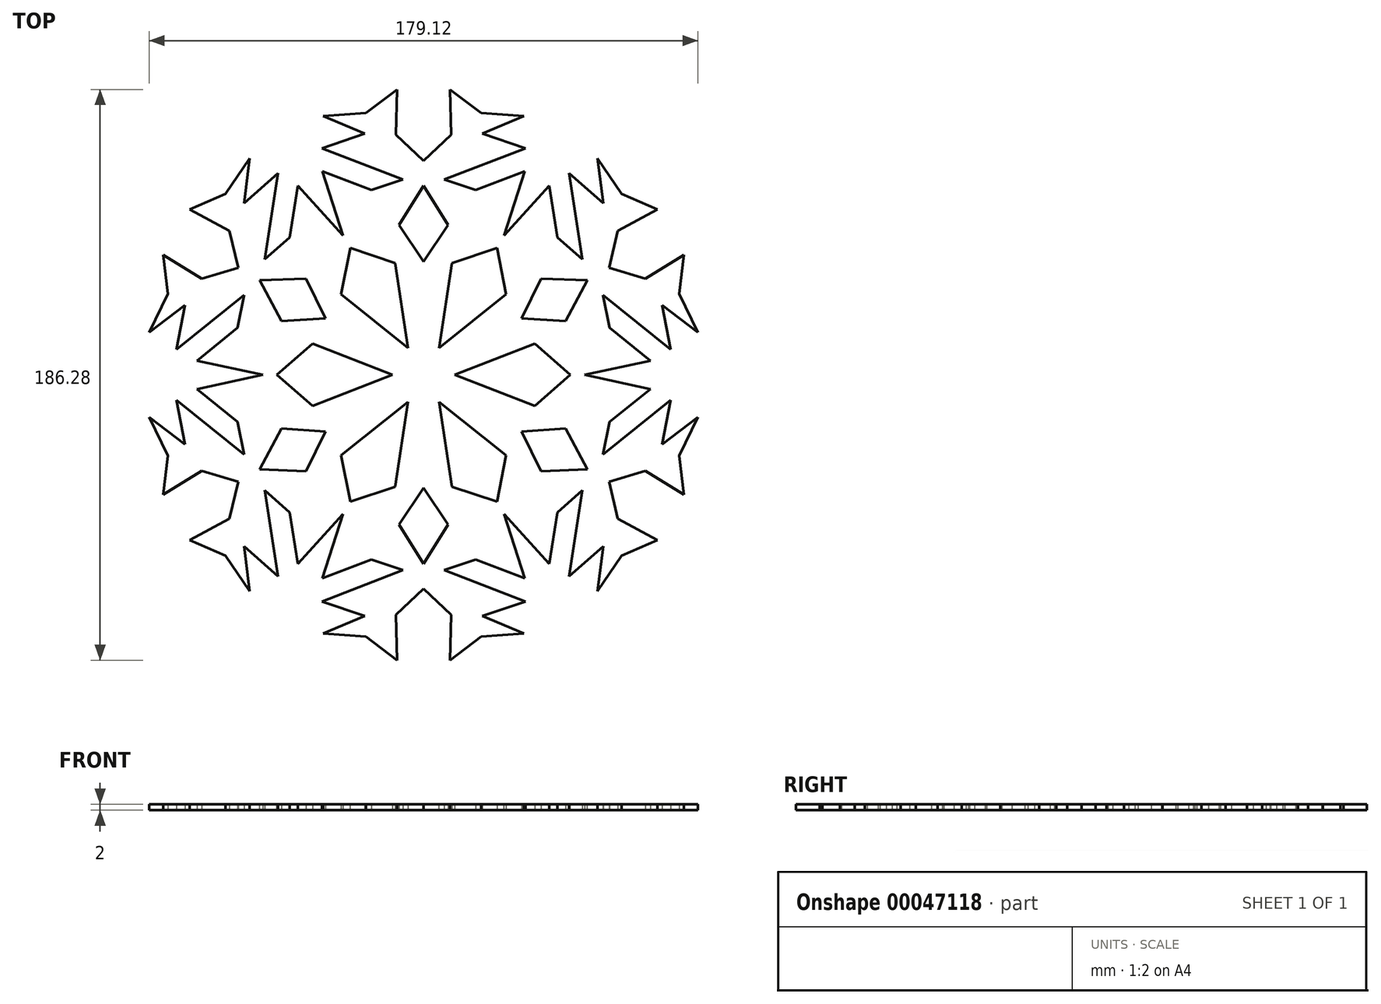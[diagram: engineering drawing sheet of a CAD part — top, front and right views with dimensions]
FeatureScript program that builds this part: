
annotation { "Feature Type Name" : "Feature", "Feature Type Description" : "" }
export const myFeature = defineFeature(function(context is Context, id is Id, definition is map)
    precondition{}
    {
        {
            var Q0;
            Q0=qCreatedBy(makeId("Top.planeOp"),FACE);
            var sketch = newSketch(context, id + "F0", { "sketchPlane" : qUnion([Q0])});
            skLineSegment(sketch, "E0", {"start": v(0, 0) * mm, "end": v(0, 95) * mm, "construction": true});
            skLineSegment(sketch, "E1", {"start": v(8.05, 48.91) * mm, "end": v(-3.23, 66.82) * mm});
            skLineSegment(sketch, "E2", {"start": v(-3.23, 66.82) * mm, "end": v(9, 78.36) * mm});
            skLineSegment(sketch, "E3", {"start": v(9, 78.36) * mm, "end": v(8.6, 93.14) * mm});
            skLineSegment(sketch, "E4", {"start": v(8.6, 93.14) * mm, "end": v(18.82, 85.46) * mm});
            skLineSegment(sketch, "E5", {"start": v(18.82, 85.46) * mm, "end": v(32.8, 84.48) * mm});
            skLineSegment(sketch, "E6", {"start": v(32.8, 84.48) * mm, "end": v(19.22, 78.78) * mm});
            skLineSegment(sketch, "E7", {"start": v(19.22, 78.78) * mm, "end": v(33.21, 73.99) * mm});
            skLineSegment(sketch, "E8", {"start": v(33.21, 73.99) * mm, "end": v(6.72, 63.73) * mm});
            skLineSegment(sketch, "E9", {"start": v(6.72, 63.73) * mm, "end": v(17.05, 60.28) * mm});
            skLineSegment(sketch, "E10", {"start": v(17.05, 60.28) * mm, "end": v(32.99, 66.38) * mm});
            skLineSegment(sketch, "E11", {"start": v(32.99, 66.38) * mm, "end": v(25.08, 41.83) * mm});
            skLineSegment(sketch, "E12", {"start": v(9.3, 36.5) * mm, "end": v(25.08, 41.83) * mm});
            skLineSegment(sketch, "E13", {"start": v(9.3, 36.5) * mm, "end": v(3.76, 0) * mm});
            skLineSegment(sketch, "E14", {"start": v(3.76, 0) * mm, "end": v(0, 0) * mm});
            skLineSegment(sketch, "E15", {"start": v(0, 0) * mm, "end": v(0, 13.61) * mm});
            skLineSegment(sketch, "E16", {"start": v(0, 13.61) * mm, "end": v(-2.1, 33.85) * mm});
            skLineSegment(sketch, "E17", {"start": v(-2.1, 33.85) * mm, "end": v(8.05, 48.91) * mm});
            skSolve(sketch);
        }
        {
            var Q0;
            Q0=qSketchRegion(id+"F0",true);
            extrude(context, id + "F1", {"entities" : qUnion([Q0]), "depth" : 2 * mm});
        }
        {
            var Q0;
            Q0=makeQuery(id+"F1.opExtrude","SWEPT_BODY",BODY,{"disambiguationData":[OSD([sQuery(id+"F0.wireOp",EDGE,"E1"),sQuery(id+"F0.wireOp",EDGE,"E2"),sQuery(id+"F0.wireOp",EDGE,"E3"),sQuery(id+"F0.wireOp",EDGE,"E4"),sQuery(id+"F0.wireOp",EDGE,"e0bc6914-2f17-417e-814f-d7e3601135d1"),sQuery(id+"F0.wireOp",EDGE,"E5"),sQuery(id+"F0.wireOp",EDGE,"E6"),sQuery(id+"F0.wireOp",EDGE,"E7"),sQuery(id+"F0.wireOp",EDGE,"E8"),sQuery(id+"F0.wireOp",EDGE,"E9"),sQuery(id+"F0.wireOp",EDGE,"E10"),sQuery(id+"F0.wireOp",EDGE,"E11"),sQuery(id+"F0.wireOp",EDGE,"E12"),sQuery(id+"F0.wireOp",EDGE,"E13"),sQuery(id+"F0.wireOp",EDGE,"E14"),sQuery(id+"F0.wireOp",EDGE,"E15"),sQuery(id+"F0.wireOp",EDGE,"E16"),sQuery(id+"F0.wireOp",EDGE,"E17")])]});
            var Q1;
            Q1=qCreatedBy(makeId("Right.planeOp"),FACE);
            mirror(context, id + "F2", {"operationType" : NewBodyOperationType.ADD, "entities" : qUnion([Q0]), "mirrorPlane" : qUnion([Q1])});
        }
        {
            var Q0;
            Q0=qCreatedBy(makeId("Front.planeOp"),FACE);
            var sketch = newSketch(context, id + "F3", { "sketchPlane" : qUnion([Q0])});
            skLineSegment(sketch, "E18", {"start": v(0, 0) * mm, "end": v(0, 8.23) * mm});
            skSolve(sketch);
        }
        {
            var Q0;
            Q0=makeQuery(id+"F1.opExtrude","SWEPT_BODY",BODY,{"disambiguationData":[OSD([sQuery(id+"F0.wireOp",EDGE,"E1"),sQuery(id+"F0.wireOp",EDGE,"E2"),sQuery(id+"F0.wireOp",EDGE,"E3"),sQuery(id+"F0.wireOp",EDGE,"E4"),sQuery(id+"F0.wireOp",EDGE,"e0bc6914-2f17-417e-814f-d7e3601135d1"),sQuery(id+"F0.wireOp",EDGE,"E5"),sQuery(id+"F0.wireOp",EDGE,"E6"),sQuery(id+"F0.wireOp",EDGE,"E7"),sQuery(id+"F0.wireOp",EDGE,"E8"),sQuery(id+"F0.wireOp",EDGE,"E9"),sQuery(id+"F0.wireOp",EDGE,"E10"),sQuery(id+"F0.wireOp",EDGE,"E11"),sQuery(id+"F0.wireOp",EDGE,"E12"),sQuery(id+"F0.wireOp",EDGE,"E13"),sQuery(id+"F0.wireOp",EDGE,"E14"),sQuery(id+"F0.wireOp",EDGE,"E15"),sQuery(id+"F0.wireOp",EDGE,"E16"),sQuery(id+"F0.wireOp",EDGE,"E17")])]});
            var Q1;
            Q1=sQuery(id+"F3.wireOp",EDGE,"E18");
            circularPattern(context, id + "F4", {"operationType" : NewBodyOperationType.ADD, "entities" : qUnion([Q0]), "axis" : qUnion([Q1]), "angle" : 60 * degree, "instanceCount" : round(6)});
        }
    });
